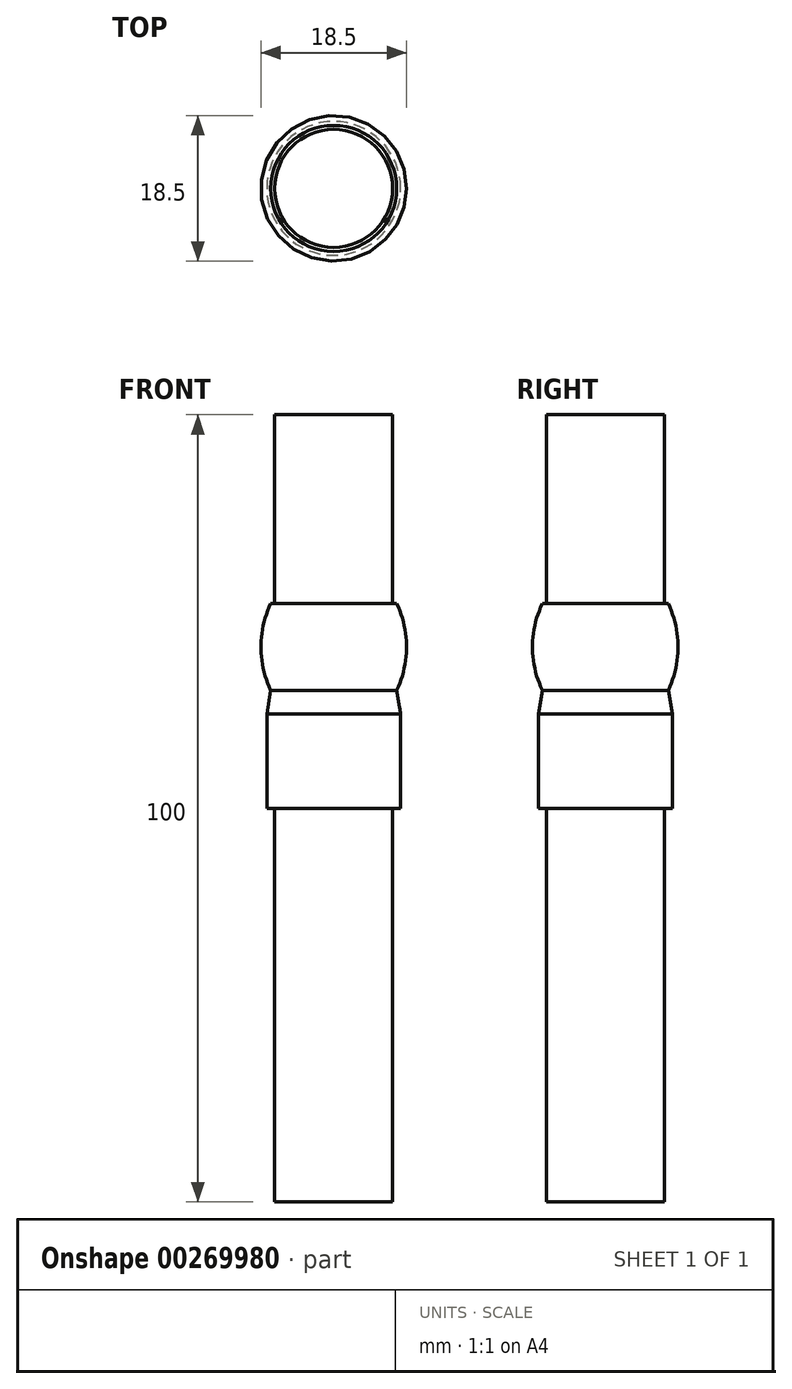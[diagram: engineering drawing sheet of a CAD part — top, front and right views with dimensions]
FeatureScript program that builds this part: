
annotation { "Feature Type Name" : "Feature", "Feature Type Description" : "" }
export const myFeature = defineFeature(function(context is Context, id is Id, definition is map)
    precondition{}
    {
        {
            var Q0;
            Q0=qCreatedBy(makeId("Top.planeOp"),FACE);
            var sketch = newSketch(context, id + "F0", { "sketchPlane" : qUnion([Q0])});
            skCircle(sketch, "E0", {"center": v(0, 0) * mm, "radius": 7.5 * mm});
            skSolve(sketch);
        }
        {
            var Q0;
            Q0=makeQuery(id+"F0.imprint","IMPRINT",FACE,{"disambiguationData":[TD([[makeQuery(id+"F0.imprint","IMPRINT",EDGE,{"derivedFrom":sQuery(id+"F0.wireOp",EDGE,"E0")}),1.0]])]});
            extrude(context, id + "F1", {"entities" : qUnion([Q0]), "depth" : 50 * mm, "hasSecondDirection" : true, "secondDirectionOppositeDirection" : true, "secondDirectionDepth" : 50 * mm});
        }
        {
            var Q0;
            Q0=qCreatedBy(makeId("Top.planeOp"),FACE);
            var sketch = newSketch(context, id + "F2", { "sketchPlane" : qUnion([Q0])});
            skCircle(sketch, "E1", {"center": v(0, 0) * mm, "radius": 8.5 * mm});
            skCircle(sketch, "E2", {"center": v(0, 0) * mm, "radius": 7.5 * mm});
            skSolve(sketch);
        }
        {
            var Q0;
            Q0=makeQuery(id+"F2.imprint","IMPRINT",FACE,{"disambiguationData":[TD([[makeQuery(id+"F2.imprint","IMPRINT",EDGE,{"derivedFrom":sQuery(id+"F2.wireOp",EDGE,"E1")}),1.0]])]});
            extrude(context, id + "F3", {"entities" : qUnion([Q0]), "depth" : 12 * mm});
        }
        {
            var Q0;
            Q0=qCreatedBy(makeId("Front.planeOp"),FACE);
            var sketch = newSketch(context, id + "F4", { "sketchPlane" : qUnion([Q0])});
            skLineSegment(sketch, "E3", {"start": v(-7.5, 15) * mm, "end": v(-7.5, 12) * mm});
            skLineSegment(sketch, "E4", {"start": v(-7.5, 12) * mm, "end": v(-8.5, 12) * mm});
            skLineSegment(sketch, "E5", {"start": v(-8.5, 12) * mm, "end": v(-8, 15) * mm});
            skLineSegment(sketch, "E6", {"start": v(-8, 15) * mm, "end": v(-7.5, 15) * mm});
            skLineSegment(sketch, "E7", {"start": v(-7.5, 15) * mm, "end": v(-7.5, 22) * mm});
            skLineSegment(sketch, "E8", {"start": v(-7.5, 26) * mm, "end": v(-8, 26) * mm});
            skPoint(sketch, "E9", {"position": v(-7.5, 20.5) * mm});
            skLineSegment(sketch, "E10", {"start": v(-7.5, 20.5) * mm, "end": v(-9.25, 20.5) * mm, "construction": true});
            skArc(sketch, "E11", {"start": v(-8, 26) * mm, "mid": v(-9.25, 20.5) * mm, "end": v(-8, 15) * mm});
            skPoint(sketch, "E12", {"position": v(-7.5, 22) * mm});
            skLineSegment(sketch, "E13", {"start": v(-7.5, 26) * mm, "end": v(-6.75, 26) * mm});
            skLineSegment(sketch, "E14", {"start": v(-6.75, 26) * mm, "end": v(-6.75, 22) * mm});
            skLineSegment(sketch, "E15", {"start": v(-6.75, 22) * mm, "end": v(-7.5, 22) * mm});
            skLineSegment(sketch, "E16", {"start": v(0, 40.64) * mm, "end": v(0, 24.11) * mm, "construction": true});
            skSolve(sketch);
        }
        {
            var Q0;
            Q0=makeQuery(id+"F4.imprint","IMPRINT",FACE,{"disambiguationData":[TD([[makeQuery(id+"F4.imprint","IMPRINT",EDGE,{"derivedFrom":sQuery(id+"F4.wireOp",EDGE,"E6")}),1.0]])]});
            var Q1;
            Q1=makeQuery(id+"F4.imprint","IMPRINT",FACE,{"disambiguationData":[TD([[makeQuery(id+"F4.imprint","IMPRINT",EDGE,{"derivedFrom":sQuery(id+"F4.wireOp",EDGE,"E3")}),-1.0]])]});
            var Q2;
            Q2=sQuery(id+"F4.wireOp",EDGE,"E16");
            revolve(context, id + "F5", {"operationType" : NewBodyOperationType.ADD, "entities" : qUnion([Q0, Q1]), "axis" : qUnion([Q2]), "revolveType" : RevolveType.FULL});
        }
    });
